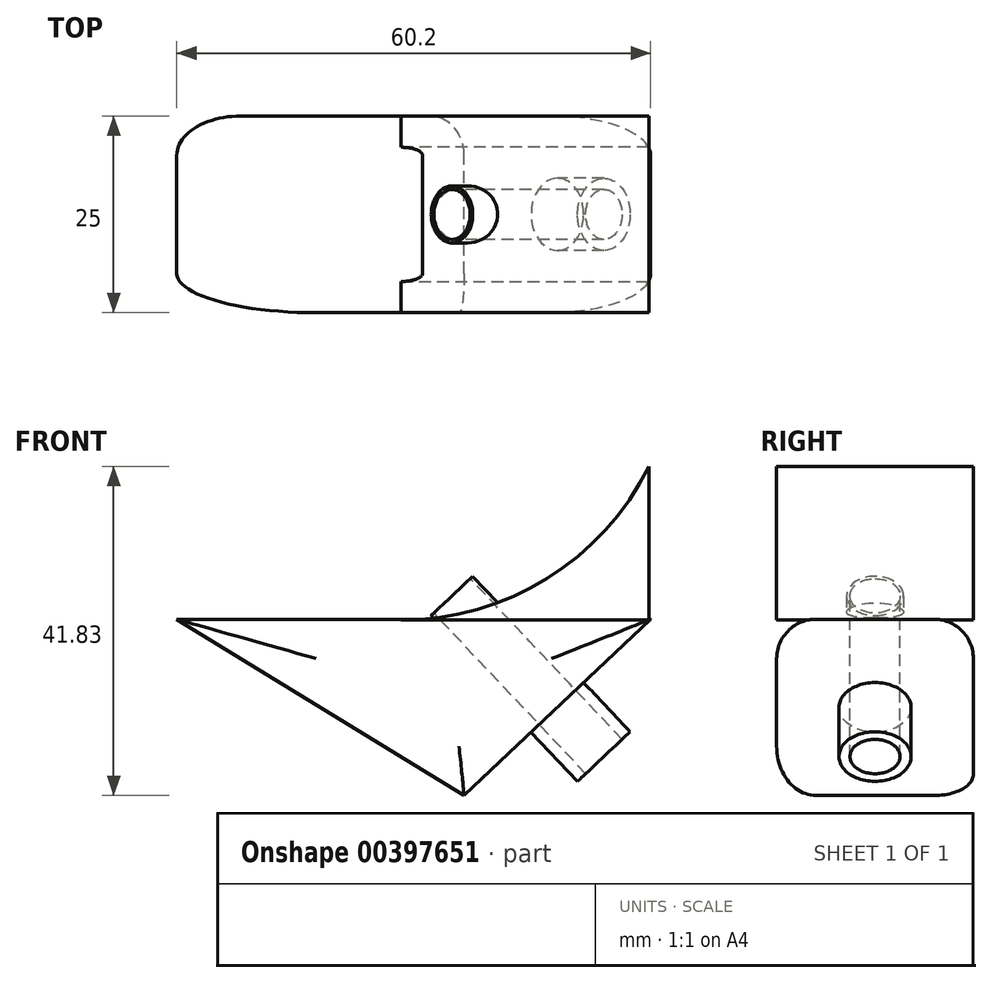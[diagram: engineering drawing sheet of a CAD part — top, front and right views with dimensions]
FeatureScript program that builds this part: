
annotation { "Feature Type Name" : "Feature", "Feature Type Description" : "" }
export const myFeature = defineFeature(function(context is Context, id is Id, definition is map)
    precondition{}
    {
        {
            var Q0;
            Q0=qCreatedBy(makeId("Front.planeOp"),FACE);
            var sketch = newSketch(context, id + "F0", { "sketchPlane" : qUnion([Q0])});
            skLineSegment(sketch, "E0", {"start": v(0, 0) * mm, "end": v(23.69, 22.4) * mm});
            skLineSegment(sketch, "E1", {"start": v(23.69, 22.4) * mm, "end": v(-36.51, 22.4) * mm});
            skLineSegment(sketch, "E2", {"start": v(-36.51, 22.4) * mm, "end": v(0, 0) * mm});
            skSolve(sketch);
        }
        {
            var Q0;
            Q0=makeQuery(id+"F0.imprint","IMPRINT",FACE,{"disambiguationData":[TD([[makeQuery(id+"F0.imprint","IMPRINT",EDGE,{"derivedFrom":sQuery(id+"F0.wireOp",EDGE,"E0")}),1.0]])]});
            extrude(context, id + "F1", {"entities" : qUnion([Q0]), "depth" : 25 * mm});
        }
        {
            var Q0;
            Q0=makeQuery(id+"F1.opExtrude","CAP_EDGE",EDGE,{"disambiguationData":[OSD([sQuery(id+"F0.wireOp",EDGE,"E0")])],"isStart":false});
            var Q1;
            Q1=makeQuery(id+"F1.opExtrude","CAP_EDGE",EDGE,{"disambiguationData":[OSD([sQuery(id+"F0.wireOp",EDGE,"E0")])],"isStart":true});
            var Q2;
            Q2=makeQuery(id+"F1.opExtrude","CAP_EDGE",EDGE,{"disambiguationData":[OSD([sQuery(id+"F0.wireOp",EDGE,"E2")])],"isStart":false});
            var Q3;
            Q3=makeQuery(id+"F1.opExtrude","CAP_EDGE",EDGE,{"disambiguationData":[OSD([sQuery(id+"F0.wireOp",EDGE,"E1")])],"isStart":true});
            var Q4;
            Q4=makeQuery(id+"F1.opExtrude","CAP_EDGE",EDGE,{"disambiguationData":[OSD([sQuery(id+"F0.wireOp",EDGE,"E1")])],"isStart":false});
            fillet(context, id + "F2", {"entities" : qUnion([Q0, Q1, Q2, Q3, Q4]), "radius" : 5 * mm, "tangentPropagation" : true, "allowEdgeOverflow" : false});
        }
        {
            var Q0;
            Q0=qCreatedBy(makeId("Front.planeOp"),FACE);
            var sketch = newSketch(context, id + "F3", { "sketchPlane" : qUnion([Q0])});
            skLineSegment(sketch, "E3.bottom", {"start": v(23.48, 22.29) * mm, "end": v(23.53, 22.29) * mm});
            skLineSegment(sketch, "E3.top", {"start": v(23.48, 41.9) * mm, "end": v(23.53, 41.9) * mm});
            skLineSegment(sketch, "E3.left", {"start": v(23.48, 22.29) * mm, "end": v(23.48, 41.9) * mm});
            skLineSegment(sketch, "E3.right", {"start": v(23.53, 22.29) * mm, "end": v(23.53, 41.9) * mm});
            skLineSegment(sketch, "E4", {"start": v(23.53, 22.29) * mm, "end": v(-8.03, 22.29) * mm});
            skArc(sketch, "E5", {"start": v(-8.03, 22.29) * mm, "mid": v(10.55, 27.6) * mm, "end": v(23.53, 41.9) * mm});
            skSolve(sketch);
        }
        {
            var Q0;
            {var subQ0=sQuery(id+"F3.wireOp",EDGE,"E4");var subQ1=sQuery(id+"F3.wireOp",EDGE,"E3.left");var subQ2=makeQuery(id+"F3.imprint","INTERSECT",VERTEX,{"derivedFrom":[subQ1,subQ0]});Q0=makeQuery(id+"F3.imprint","IMPRINT",FACE,{"disambiguationData":[TD([[makeQuery(id+"F3.imprint","IMPRINT",EDGE,{"disambiguationData":[TD([[subQ2,-1.0]])],"derivedFrom":subQ1}),1.0]])]});}
            extrude(context, id + "F4", {"entities" : qUnion([Q0]), "operationType" : NewBodyOperationType.ADD, "depth" : 25 * mm});
        }
        {
            var Q0;
            Q0=makeQuery(id+"F1.opExtrude","SWEPT_FACE",FACE,{"disambiguationData":[OSD([sQuery(id+"F0.wireOp",EDGE,"E0")])]});
            var sketch = newSketch(context, id + "F5", { "sketchPlane" : qUnion([Q0])});
            skCircle(sketch, "E6", {"center": v(16.3, 12.5) * mm, "radius": 4.59 * mm});
            skPoint(sketch, "E6.centerSnap0", {"position": v(0, 12.5) * mm});
            skPoint(sketch, "E6.centerSnap1", {"position": v(16.3, 5) * mm});
            skSolve(sketch);
        }
        {
            var Q0;
            Q0=makeQuery(id+"F5.imprint","IMPRINT",FACE,{"disambiguationData":[TD([[makeQuery(id+"F5.imprint","IMPRINT",EDGE,{"derivedFrom":sQuery(id+"F5.wireOp",EDGE,"E6")}),1.0]])]});
            extrude(context, id + "F6", {"entities" : qUnion([Q0]), "operationType" : NewBodyOperationType.ADD, "depth" : 8.6 * mm});
        }
        {
            var Q0;
            Q0=makeQuery(id+"F6.opExtrude","CAP_FACE",FACE,{"disambiguationData":[OSD([sQuery(id+"F5.wireOp",EDGE,"E6")])],"isStart":false});
            var sketch = newSketch(context, id + "F7", { "sketchPlane" : qUnion([Q0])});
            skCircle(sketch, "E7", {"center": v(16.3, 12.5) * mm, "radius": 3.62 * mm});
            skSolve(sketch);
        }
        {
            var Q0;
            Q0 = qSketchRegion(id + "F7", true);
            extrude(context, id + "F8", {"entities" : qUnion([Q0]), "operationType" : NewBodyOperationType.ADD, "oppositeDirection" : true, "depth" : 28.09 * mm});
        }
        {
            var Q0;
            Q0=makeQuery(id+"F8.opExtrude","CAP_FACE",FACE,{"disambiguationData":[OSD([sQuery(id+"F7.wireOp",EDGE,"E7")])],"isStart":false});
            var sketch = newSketch(context, id + "F9", { "sketchPlane" : qUnion([Q0])});
            skCircle(sketch, "E8", {"center": v(16.3, -12.5) * mm, "radius": 3.18 * mm});
            skSolve(sketch);
        }
        {
            var Q0;
            Q0 = qSketchRegion(id + "F9", true);
            extrude(context, id + "F10", {"entities" : qUnion([Q0]), "operationType" : NewBodyOperationType.REMOVE, "oppositeDirection" : true, "depth" : 44.3 * mm});
        }
    });
